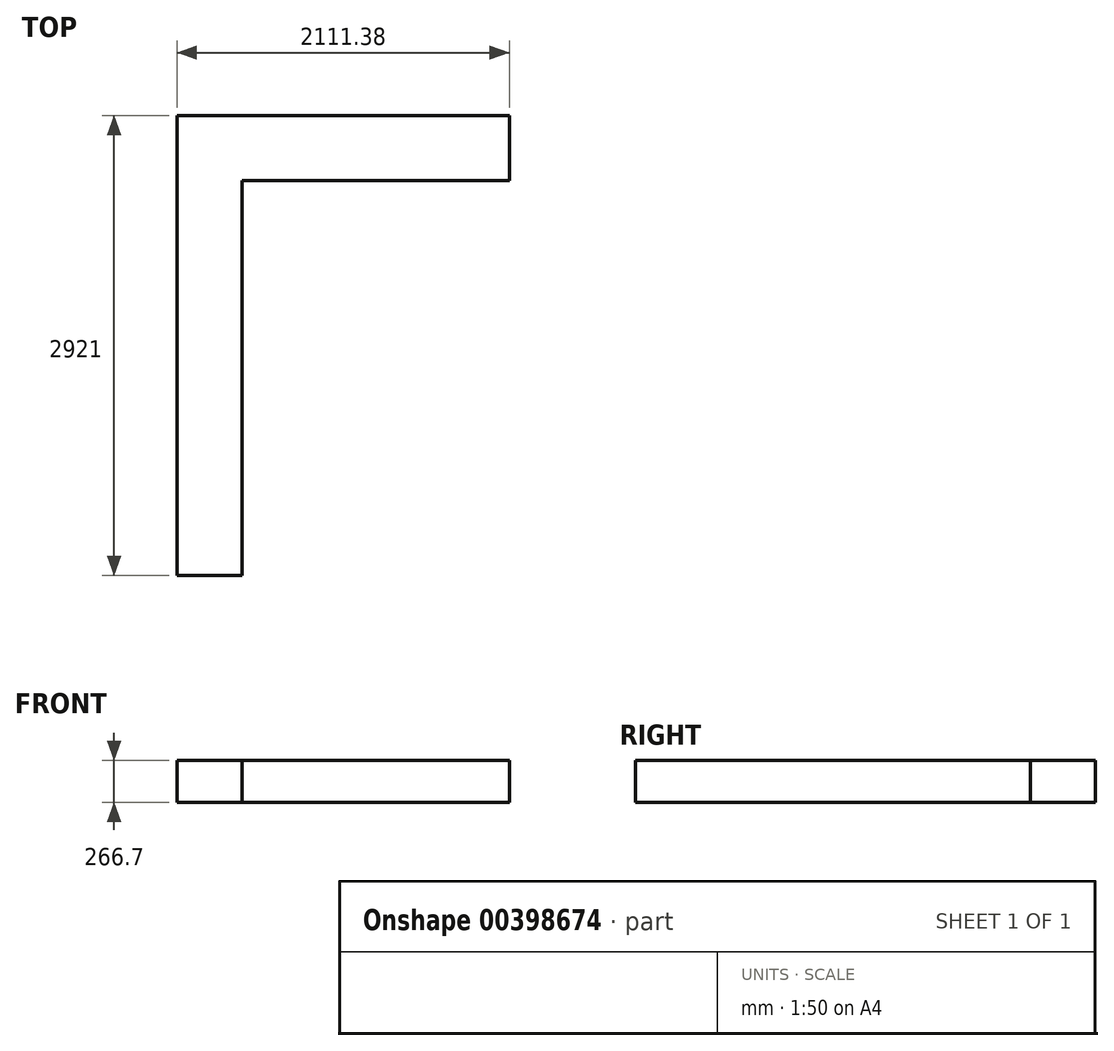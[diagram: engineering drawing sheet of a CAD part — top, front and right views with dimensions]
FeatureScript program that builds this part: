
annotation { "Feature Type Name" : "Feature", "Feature Type Description" : "" }
export const myFeature = defineFeature(function(context is Context, id is Id, definition is map)
    precondition{}
    {
        {
            var Q0;
            Q0=qCreatedBy(makeId("Top.planeOp"),FACE);
            var sketch = newSketch(context, id + "F0", { "sketchPlane" : qUnion([Q0])});
            skLineSegment(sketch, "E0", {"start": v(0, 0) * mm, "end": v(412.75, 0) * mm});
            skLineSegment(sketch, "E1", {"start": v(412.75, 0) * mm, "end": v(412.75, 2508.25) * mm});
            skLineSegment(sketch, "E2", {"start": v(412.75, 2508.25) * mm, "end": v(2111.38, 2508.25) * mm});
            skLineSegment(sketch, "E3", {"start": v(2111.38, 2508.25) * mm, "end": v(2111.38, 2921) * mm});
            skLineSegment(sketch, "E4", {"start": v(2111.38, 2921) * mm, "end": v(0, 2921) * mm});
            skLineSegment(sketch, "E5", {"start": v(0, 2921) * mm, "end": v(0, 0) * mm});
            skSolve(sketch);
        }
        {
            var Q0;
            Q0 = qSketchRegion(id + "F0", true);
            extrude(context, id + "F1", {"entities" : qUnion([Q0]), "depth" : 266.7 * mm});
        }
    });
